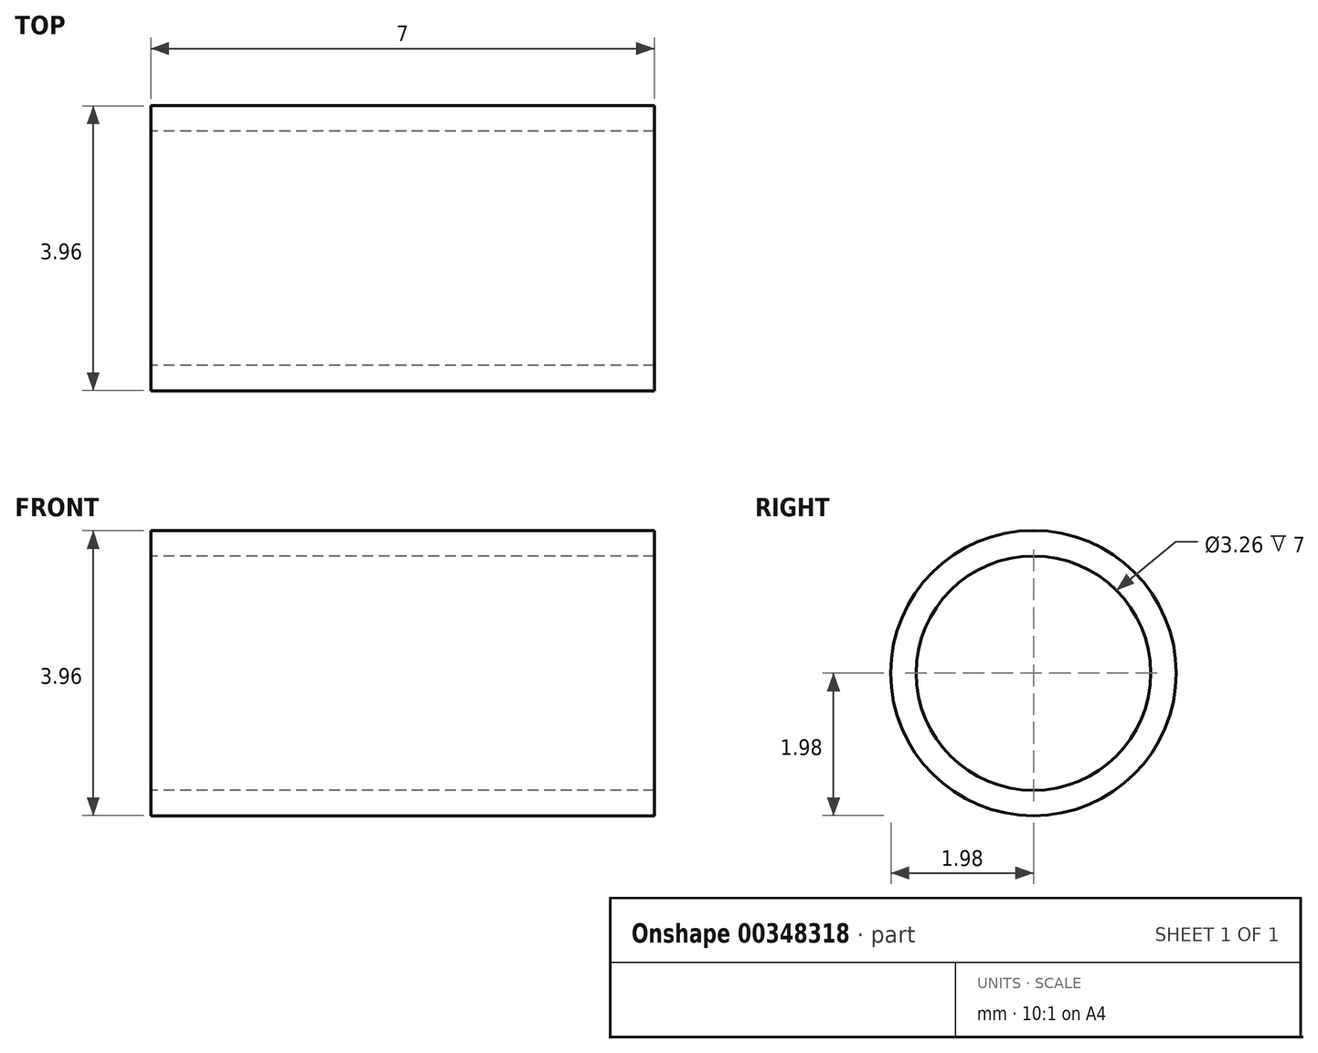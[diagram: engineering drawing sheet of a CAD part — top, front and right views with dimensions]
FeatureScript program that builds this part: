
annotation { "Feature Type Name" : "Feature", "Feature Type Description" : "" }
export const myFeature = defineFeature(function(context is Context, id is Id, definition is map)
    precondition{}
    {
        {
            var Q0;
            Q0=qCreatedBy(makeId("Right.planeOp"),FACE);
            var sketch = newSketch(context, id + "F0", { "sketchPlane" : qUnion([Q0])});
            skCircle(sketch, "E0", {"center": v(0, 0) * mm, "radius": 1.63 * mm});
            skCircle(sketch, "E1", {"center": v(0, 0) * mm, "radius": 1.98 * mm});
            skCircle(sketch, "E2", {"center": v(0, 0) * mm, "radius": 1.59 * mm, "construction": true});
            skSolve(sketch);
        }
        {
            var Q0;
            Q0 = qSketchRegion(id + "F0", true);
            extrude(context, id + "F1", {"entities" : qUnion([Q0]), "depth" : 7 * mm, "symmetric" : true});
        }
    });
